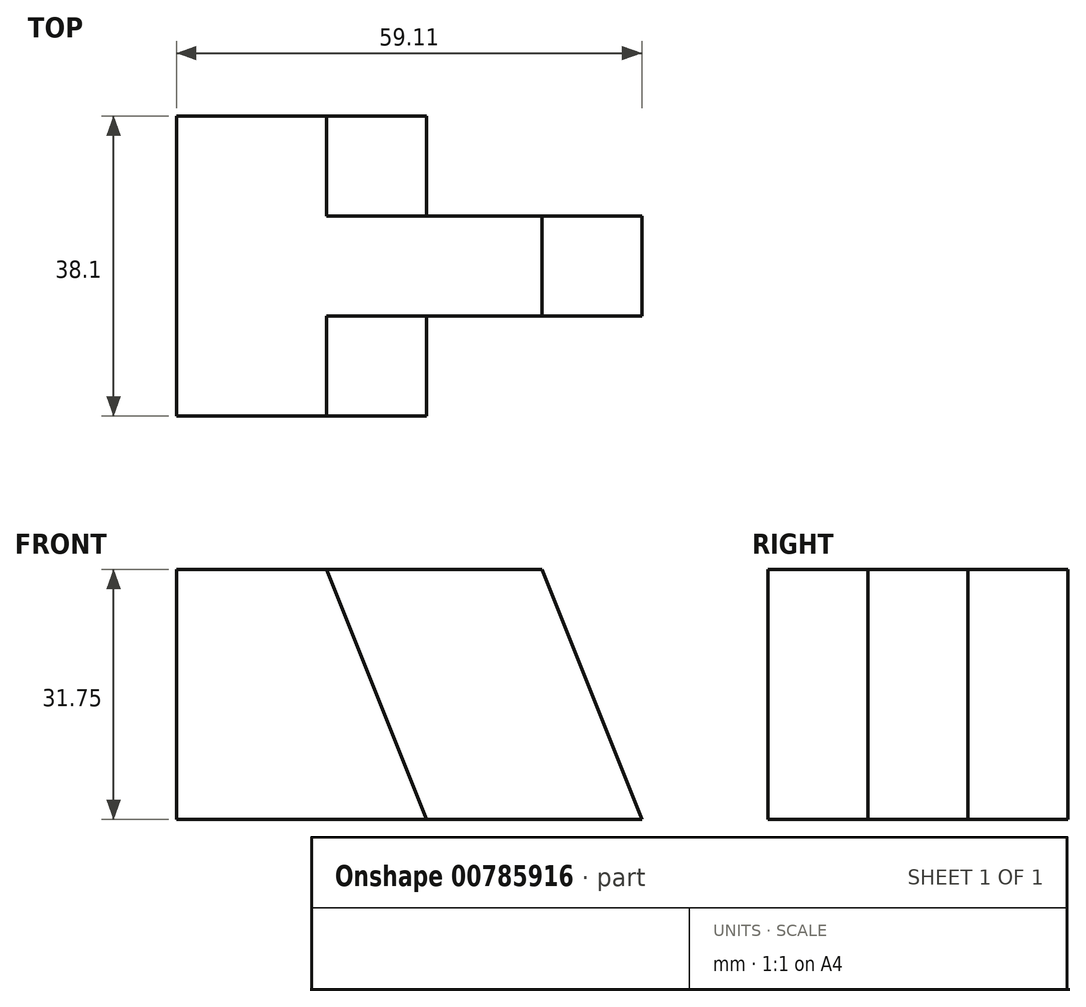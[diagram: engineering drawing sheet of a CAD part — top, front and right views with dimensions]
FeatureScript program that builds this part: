
annotation { "Feature Type Name" : "Feature", "Feature Type Description" : "" }
export const myFeature = defineFeature(function(context is Context, id is Id, definition is map)
    precondition{}
    {
        {
            var Q0;
            Q0=qCreatedBy(makeId("Front.planeOp"),FACE);
            var sketch = newSketch(context, id + "F0", { "sketchPlane" : qUnion([Q0])});
            skLineSegment(sketch, "E0", {"start": v(0, 0) * mm, "end": v(31.75, 0) * mm});
            skLineSegment(sketch, "E1", {"start": v(0, 0) * mm, "end": v(0, 31.75) * mm});
            skLineSegment(sketch, "E2", {"start": v(0, 31.75) * mm, "end": v(19.05, 31.75) * mm});
            skLineSegment(sketch, "E3", {"start": v(19.05, 31.75) * mm, "end": v(31.75, 0) * mm});
            skSolve(sketch);
        }
        {
            var Q0;
            Q0=makeQuery(id+"F0.imprint","IMPRINT",FACE,{"disambiguationData":[TD([[makeQuery(id+"F0.imprint","IMPRINT",EDGE,{"derivedFrom":sQuery(id+"F0.wireOp",EDGE,"E0")}),1.0]])]});
            extrude(context, id + "F1", {"entities" : qUnion([Q0]), "depth" : 38.1 * mm, "offsetDistance" : 25.4 * mm});
        }
        {
            var Q0;
            Q0=makeQuery(id+"F1.opExtrude","SWEPT_FACE",FACE,{"disambiguationData":[OSD([sQuery(id+"F0.wireOp",EDGE,"E3")])]});
            var sketch = newSketch(context, id + "F2", { "sketchPlane" : qUnion([Q0])});
            skLineSegment(sketch, "E4", {"start": v(-38.1, -11.8) * mm, "end": v(-25.4, -11.8) * mm});
            skLineSegment(sketch, "E5", {"start": v(-25.4, -11.8) * mm, "end": v(-25.4, 22.4) * mm});
            skLineSegment(sketch, "E6", {"start": v(-25.4, 22.4) * mm, "end": v(-12.7, 22.4) * mm});
            skLineSegment(sketch, "E7", {"start": v(-12.7, 22.4) * mm, "end": v(-12.7, -11.8) * mm});
            skSolve(sketch);
        }
        {
            var Q0;
            {var subQ0=sQuery(id+"F2.wireOp",EDGE,"E5");Q0=makeQuery(id+"F2.imprint","IMPRINT",FACE,{"disambiguationData":[TD([[makeQuery(id+"F2.imprint","IMPRINT",EDGE,{"derivedFrom":subQ0}),-1.0]])]});}
            extrude(context, id + "F3", {"entities" : qUnion([Q0]), "operationType" : NewBodyOperationType.ADD, "depth" : 25.4 * mm, "offsetDistance" : 25.4 * mm});
        }
        {
            var Q0;
            Q0=makeQuery(id+"F3.opExtrude","SWEPT_FACE",FACE,{"disambiguationData":[OSD([sQuery(id+"F2.wireOp",EDGE,"E5")])]});
            var sketch = newSketch(context, id + "F4", { "sketchPlane" : qUnion([Q0])});
            skLineSegment(sketch, "E8", {"start": v(55.33, 9.43) * mm, "end": v(59.1, 0) * mm});
            skLineSegment(sketch, "E9", {"start": v(59.1, 0) * mm, "end": v(31.75, 0) * mm});
            skLineSegment(sketch, "E10", {"start": v(19.05, 31.75) * mm, "end": v(46.4, 31.75) * mm});
            skSolve(sketch);
        }
        {
            var Q0;
            {var subQ0=sQuery(id+"F4.wireOp",EDGE,"E10");Q0=makeQuery(id+"F4.imprint","IMPRINT",FACE,{"disambiguationData":[TD([[makeQuery(id+"F4.imprint","IMPRINT",EDGE,{"derivedFrom":subQ0}),1.0]])]});}
            extrude(context, id + "F5", {"entities" : qUnion([Q0]), "operationType" : NewBodyOperationType.REMOVE, "oppositeDirection" : true, "depth" : 25.4 * mm, "offsetDistance" : 25.4 * mm});
        }
        {
            var Q0;
            Q0=makeQuery(id+"F3.opExtrude","SWEPT_FACE",FACE,{"disambiguationData":[OSD([sQuery(id+"F2.wireOp",EDGE,"E5")])]});
            var sketch = newSketch(context, id + "F6", { "sketchPlane" : qUnion([Q0])});
            skLineSegment(sketch, "E11", {"start": v(55.33, 9.43) * mm, "end": v(59.1, 0) * mm});
            skLineSegment(sketch, "E12", {"start": v(59.1, 0) * mm, "end": v(31.75, 0) * mm});
            skSolve(sketch);
        }
        {
            var Q0;
            Q0=makeQuery(id+"F6.imprint","IMPRINT",FACE,{"disambiguationData":[TD([[makeQuery(id+"F6.imprint","IMPRINT",EDGE,{"derivedFrom":sQuery(id+"F6.wireOp",EDGE,"E11")}),-1.0]])]});
            extrude(context, id + "F7", {"entities" : qUnion([Q0]), "operationType" : NewBodyOperationType.ADD, "oppositeDirection" : true, "depth" : 12.7 * mm, "offsetDistance" : 25.4 * mm});
        }
    });
